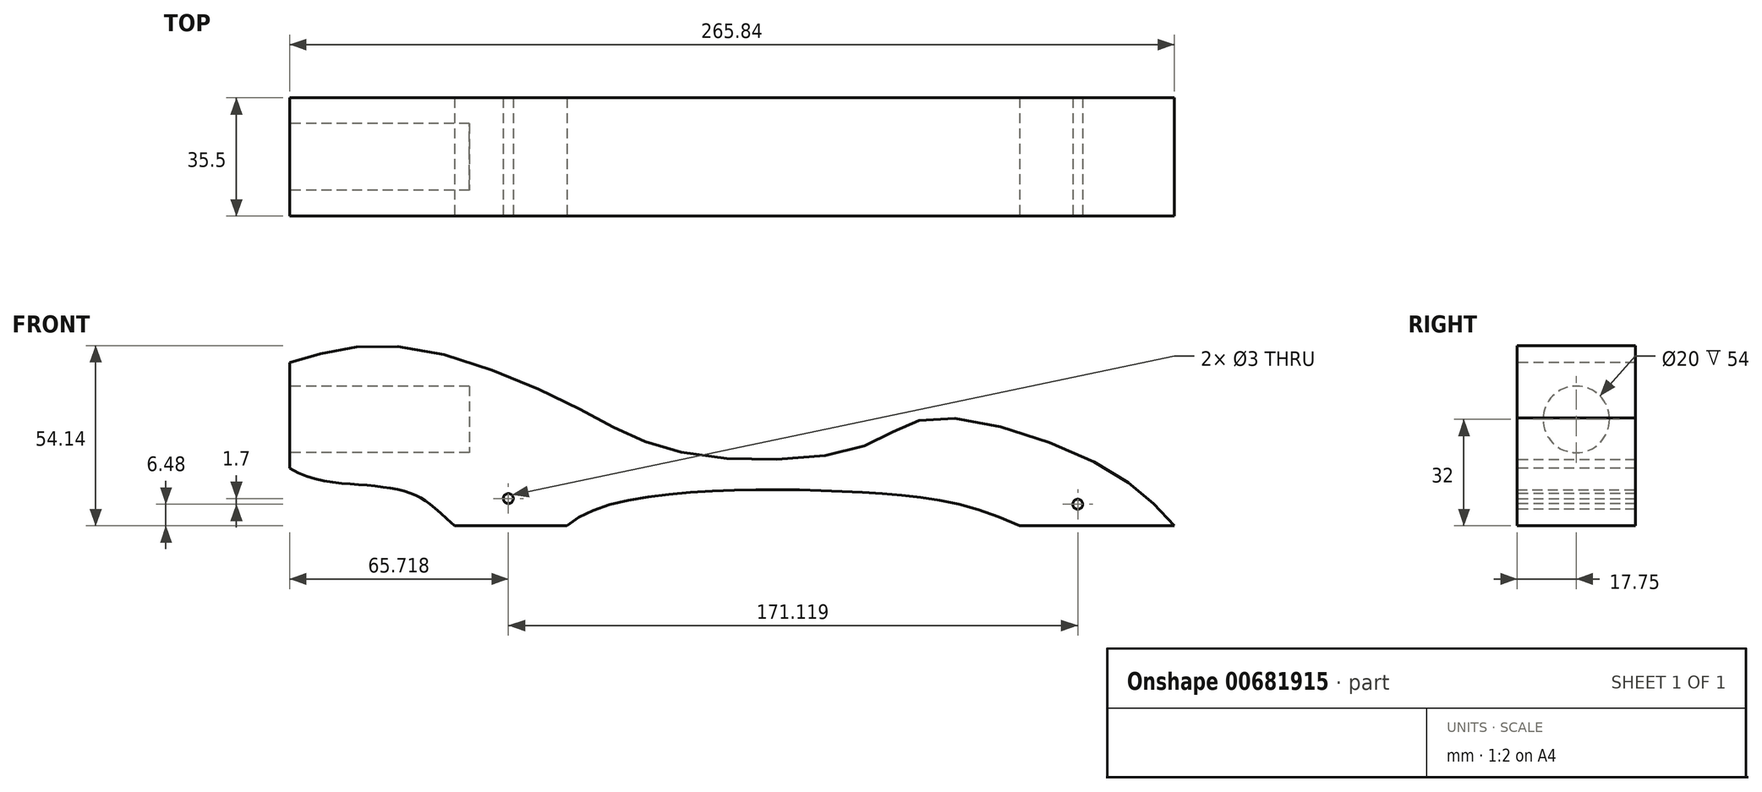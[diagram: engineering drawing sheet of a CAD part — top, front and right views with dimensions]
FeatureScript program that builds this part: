
annotation { "Feature Type Name" : "Feature", "Feature Type Description" : "" }
export const myFeature = defineFeature(function(context is Context, id is Id, definition is map)
    precondition{}
    {
        {
            var Q0;
            Q0=qCreatedBy(makeId("Front.planeOp"),FACE);
            var sketch = newSketch(context, id + "F0", { "sketchPlane" : qUnion([Q0])});
            skLineSegment(sketch, "E0.bottom", {"start": v(0, 0) * mm, "end": v(304.8, 0) * mm});
            skLineSegment(sketch, "E0.left", {"start": v(0, 0) * mm, "end": v(0, 73) * mm});
            skLineSegment(sketch, "E1", {"start": v(304.8, 0) * mm, "end": v(304.8, 19) * mm});
            skLineSegment(sketch, "E2", {"start": v(0, 73) * mm, "end": v(304.8, 19) * mm});
            skSolve(sketch);
        }
        {
            var Q0;
            Q0=makeQuery(id+"F0.imprint","IMPRINT",FACE,{"disambiguationData":[TD([[makeQuery(id+"F0.imprint","IMPRINT",EDGE,{"derivedFrom":sQuery(id+"F0.wireOp",EDGE,"E0.bottom")}),1.0]])]});
            extrude(context, id + "F1", {"entities" : qUnion([Q0]), "oppositeDirection" : true, "depth" : 42.5 * mm, "offsetDistance" : 25 * mm});
        }
        {
            var Q0;
            Q0=makeQuery(id+"F1.opExtrude","SWEPT_FACE",FACE,{"disambiguationData":[OSD([sQuery(id+"F0.wireOp",EDGE,"E0.left")])]});
            var sketch = newSketch(context, id + "F2", { "sketchPlane" : qUnion([Q0])});
            skCircle(sketch, "E3", {"center": v(-21.25, 32) * mm, "radius": 10 * mm});
            skSolve(sketch);
        }
        {
            var Q0;
            Q0=makeQuery(id+"F2.imprint","IMPRINT",FACE,{"disambiguationData":[TD([[makeQuery(id+"F2.imprint","IMPRINT",EDGE,{"derivedFrom":sQuery(id+"F2.wireOp",EDGE,"E3")}),1.0]])]});
            extrude(context, id + "F3", {"entities" : qUnion([Q0]), "operationType" : NewBodyOperationType.REMOVE, "oppositeDirection" : true, "depth" : 54 * mm, "offsetDistance" : 25 * mm});
        }
        {
            var Q0;
            Q0=makeQuery(id+"F1.opExtrude","CAP_FACE",FACE,{"disambiguationData":[OSD([sQuery(id+"F0.wireOp",EDGE,"E0.bottom"),sQuery(id+"F0.wireOp",EDGE,"E0.left"),sQuery(id+"F0.wireOp",EDGE,"E1"),sQuery(id+"F0.wireOp",EDGE,"E2")])],"isStart":true});
            var sketch = newSketch(context, id + "F4", { "sketchPlane" : qUnion([Q0])});
            skFitSpline(sketch, "E4", {"points": [v(264.55, 4.63) * mm, v(265.84, 0) * mm], "startDerivative": vector(4.03, -4.63) * mm, "endDerivative": vector(4.03, -4.63) * mm});
            skLineSegment(sketch, "E5", {"start": v(265.84, 0) * mm, "end": v(43, 0) * mm});
            skFitSpline(sketch, "E6", {"points": [v(49.63, 0) * mm, v(37.83, 9.25) * mm, v(22.8, 12.2) * mm, v(0, 17.26) * mm], "startDerivative": vector(-57.68, 51.12) * mm, "endDerivative": vector(-57.28, 34.17) * mm});
            skFitSpline(sketch, "E7", {"points": [v(83.36, 0) * mm, v(120.6, 10.07) * mm, v(173.76, 9.95) * mm, v(219.35, 0) * mm], "startDerivative": vector(71.4, 64.07) * mm, "endDerivative": vector(148.73, -69.17) * mm});
            skFitSpline(sketch, "E8", {"points": [v(0, 49.09) * mm, v(32.9, 53.9) * mm, v(87.1, 35.04) * mm, v(118.21, 22) * mm, v(171.45, 23.58) * mm, v(193, 32.31) * mm, v(244.5, 17.67) * mm, v(265.84, 0) * mm], "startDerivative": vector(196.4, 56.32) * mm, "endDerivative": vector(138.62, -158.13) * mm});
            skSolve(sketch);
        }
        {
            var Q0;
            Q0 = qSketchRegion(id + "F4", true);
            var Q1;
            {var subQ1=makeQuery(id+"F1.opExtrude","CAP_EDGE",EDGE,{"disambiguationData":[OSD([sQuery(id+"F0.wireOp",EDGE,"E1")])],"isStart":true});Q1=makeQuery(id+"F4.imprint","IMPRINT",FACE,{"disambiguationData":[TD([[makeQuery(id+"F4.imprint","IMPRINT",EDGE,{"derivedFrom":subQ1}),1.0]])]});}
            var Q2;
            {var subQ3=sQuery(id+"F4.wireOp",EDGE,"E6");Q2=makeQuery(id+"F4.imprint","IMPRINT",FACE,{"disambiguationData":[TD([[makeQuery(id+"F4.imprint","IMPRINT",EDGE,{"derivedFrom":subQ3}),1.0]])]});}
            extrude(context, id + "F5", {"entities" : qUnion([Q0, Q1, Q2]), "operationType" : NewBodyOperationType.REMOVE, "oppositeDirection" : true, "depth" : 71 * mm, "offsetDistance" : 25 * mm});
        }
        {
            var Q0;
            Q0=makeQuery(id+"F1.opExtrude","CAP_FACE",FACE,{"disambiguationData":[OSD([sQuery(id+"F0.wireOp",EDGE,"E0.bottom"),sQuery(id+"F0.wireOp",EDGE,"E0.left"),sQuery(id+"F0.wireOp",EDGE,"E1"),sQuery(id+"F0.wireOp",EDGE,"E2")])],"isStart":false});
            extrude(context, id + "F6", {"entities" : qUnion([Q0]), "operationType" : NewBodyOperationType.REMOVE, "oppositeDirection" : true, "depth" : 3.5 * mm, "offsetDistance" : 25 * mm});
        }
        {
            var Q0;
            Q0=makeQuery(id+"F1.opExtrude","CAP_FACE",FACE,{"disambiguationData":[OSD([sQuery(id+"F0.wireOp",EDGE,"E0.bottom"),sQuery(id+"F0.wireOp",EDGE,"E0.left"),sQuery(id+"F0.wireOp",EDGE,"E1"),sQuery(id+"F0.wireOp",EDGE,"E2")])],"isStart":true});
            var sketch = newSketch(context, id + "F7", { "sketchPlane" : qUnion([Q0])});
            skCircle(sketch, "E9", {"center": v(65.72, 8.18) * mm, "radius": 1.5 * mm});
            skCircle(sketch, "E10", {"center": v(236.84, 6.48) * mm, "radius": 1.5 * mm});
            skSolve(sketch);
        }
        {
            var Q0;
            Q0 = qSketchRegion(id + "F7", true);
            extrude(context, id + "F8", {"entities" : qUnion([Q0]), "operationType" : NewBodyOperationType.REMOVE, "oppositeDirection" : true, "depth" : 40 * mm, "offsetDistance" : 25 * mm});
        }
        {
            var Q0;
            Q0=makeQuery(id+"F1.opExtrude","CAP_FACE",FACE,{"disambiguationData":[OSD([sQuery(id+"F0.wireOp",EDGE,"E0.bottom"),sQuery(id+"F0.wireOp",EDGE,"E0.left"),sQuery(id+"F0.wireOp",EDGE,"E1"),sQuery(id+"F0.wireOp",EDGE,"E2")])],"isStart":true});
            extrude(context, id + "F9", {"entities" : qUnion([Q0]), "operationType" : NewBodyOperationType.REMOVE, "oppositeDirection" : true, "depth" : 3.5 * mm, "offsetDistance" : 25 * mm});
        }
    });
